# Revit family: SE-SU-300_GENERADO
name_source: partatom
category: Equipos especializados
units: mm (PartAtom-declared; Revit-internal decimal feet)

## family parameters
Compartido = No
Corte con vacíos al cargar = No
Cota de conector redondo = Diámetro de uso
Número OmniClass = 23.21.21.47
Punto de cálculo de habitación = No
Se basa en plano de trabajo = No
Siempre vertical = Sí
Tipo de pieza = Normal

## types (14) — shared parameters
Depth = 465 mm  [stored 1.52559 ft]
Fabricante = SAMMIC S.L.
Foodservice Equipment Identifier = Sí
Phase = 1
Revision Code = 1
URL = https://www.sammic.com
URL Cutsheet = http://www.sammic.com
Width = 384 mm  [stored 1.25984 ft]
zero-valued in all types: Elevación por defecto

## per-type parameters (varying)
| type | Comentarios de tipo | Conn Plug | Cycle | FL Amps | Height | Modelo | Specification by Manufacturer | Volts | Weight in Pounds |
| Vacuum packing machine SE-308 230/50-60/1 | Tabletop model. 8 m³/h. -- mm | EU (SCHUKO 2P+G) | 50 Hz | 3 A | 405 mm  [stored 1.32874 ft] | 1141083 | -- mm sealing bar.

8 m³/h Busch vacuum pump.

Vacuum controlled by sensor. | 230 V | 79.6 |
| Vacuum packing machine SE-310 230/50-60/1 | Tabletop model. 10 m³/h. 320 mm | EU (SCHUKO 2P+G) | 50 Hz | 3 A | 403 mm  [stored 1.32218 ft] | 1140628 | 320 mm sealing bar.

10 m³/h Busch vacuum pump.

Vacuum controlled by sensor. | 230 V | 87.1 |
| Vacuum packing machine SE-310 120/50-60/1 | Tabletop model. 12 m³/h. 320 mm | USA (NEMA 5-15P / 2P+G) | 60 Hz | 6 A | 403 mm  [stored 1.32218 ft] | 1140629 | 320 mm sealing bar.

12 m³/h Busch vacuum pump.

Vacuum controlled by sensor. | 120 V | 87.1 |
| Vacuum packing machine SE-310 230/50-60/1 AUS | Tabletop model. 10 m³/h. 320 mm | AU/NZ (AS 3112 10A / 2P+G) | 50 Hz | 3 A | 403 mm  [stored 1.32218 ft] | 1140640 | 320 mm sealing bar.

10 m³/h Busch vacuum pump.

Vacuum controlled by sensor. | 230 V | 87.1 |
| Vacuum packing machine SE-316 230/50-60/1 | Tabletop model. 16 m³/h. 320 mm | EU (SCHUKO 2P+G) | 50 Hz | 4 A | 403 mm  [stored 1.32218 ft] | 1140630 | 320 mm sealing bar.

16 m³/h Busch vacuum pump.

Vacuum controlled by sensor. | 230 V | 92.6 |
| Vacuum packing machine SE-316 120/50-60/1 | Tabletop model. 16 m³/h. 320 mm | USA (NEMA 5-15P / 2P+G) | 60 Hz | 8 A | 403 mm  [stored 1.32218 ft] | 1140631 | 320 mm sealing bar.

16 m³/h Busch vacuum pump.

Vacuum controlled by sensor. | 120 V | 92.6 |
| Vacuum packing machine SE-306 230/50-60/1 | Tabletop model. 6 m³/h. 320 mm. | EU (SCHUKO 2P+G) | 50 Hz | 4 A | 405 mm  [stored 1.32874 ft] | 1140626 | 320 mm. sealing bar.
6 m³/h Busch vacuum pump.
Vacuum controlled by sensor. | 230 V | 79.6 |
| Vacuum packing machine SU-310 230/50-60/1 | Tabletop model. 10 m³/h. 320 mm. | EU (SCHUKO 2P+G) | 50 Hz | 3 A | 403 mm  [stored 1.32218 ft] | 1140730 | 320 mm. sealing bar.
10 m³/h Busch vacuum pump.
Vacuum controlled by sensor. | 230 V | 87.1 |
| Vacuum packing machine SU-310P 230/50-60/1 | Tabletop model. 10 m³/h. 320 mm. | EU (SCHUKO 2P+G) | 50 Hz | 3 A | 403 mm  [stored 1.32218 ft] | 1140732 | 320 mm. sealing bar.
10 m³/h Busch vacuum pump.
Vacuum controlled by sensor. | 230 V | 87.1 |
| Vacuum packing machine SU-310P 120/50-60/1 | Tabletop model. 10 m³/h. 320 mm. | USA (NEMA 5-15P / 2P+G) | 60 Hz | 6 A | 403 mm  [stored 1.32218 ft] | 1140737 | 320 mm. sealing bar.
10 m³/h Busch vacuum pump.
Vacuum controlled by sensor. | 120 V | 87.1 |
| Vacuum packing machine SU-316 230/50-60/1 | Tabletop model. 16 m³/h. 320 mm. | EU (SCHUKO 2P+G) | 50 Hz | 4 A | 403 mm  [stored 1.32218 ft] | 1140742 | 320 mm. sealing bar.
16 m³/h Busch vacuum pump.
Vacuum controlled by sensor. | 230 V | 92.6 |
| Vacuum packing machine SU-316P 230/50-60/1 | Tabletop model. 16 m³/h. 320 mm. | EU (SCHUKO 2P+G) | 50 Hz | 4 A | 403 mm  [stored 1.32218 ft] | 1140744 | 320 mm. sealing bar.
16 m³/h Busch vacuum pump.
Vacuum controlled by sensor. | 230 V | 92.6 |
| Vacuum packing machine SU-316P+ 230/50-60/1 | Tabletop model. 16 m³/h. 320 mm. | EU (SCHUKO 2P+G) | 50 Hz | 4 A | 403 mm  [stored 1.32218 ft] | 1140746 | 320 mm. sealing bar.
16 m³/h Busch vacuum pump.
Vacuum controlled by sensor. | 230 V | 92.6 |
| Vacuum packing machine SU-316P+ 120/50-60/1 (with PLUS welding option) | Tabletop model. 16 m³/h. 320 mm. | USA (NEMA 5-15P / 2P+G) | 60 Hz | 8 A | 403 mm  [stored 1.32218 ft] | 1140755 | 320 mm. sealing bar.
16 m³/h Busch vacuum pump.
Vacuum controlled by sensor. | 120 V | 92.6 |

note: column(s) folded — value = type name in every type: Descripción

note: [stored X ft] marks values corroborated as IEEE doubles in the binary element streams (Revit-internal decimal feet)
